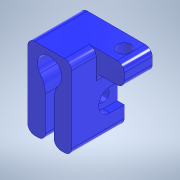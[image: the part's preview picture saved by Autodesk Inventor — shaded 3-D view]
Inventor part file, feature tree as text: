
AUTODESK INVENTOR PART (.ipt)
format: ipt  version: 2022 (Build 260153000, 153)  size: 223,744 bytes
history: native  units: in
note: dims shown in document units (in); Inventor stores cm internally (conversion verified against a paired STEP export)
features: sketch x4, extrude x4, hole x3, projected_geometry x2, plane x1, fillet x1
ambient origin geometry x8: Origin, YZ Plane, XZ Plane, XY Plane, X Axis, Y Axis, Z Axis, Center Point
bodies: Body1 (feature_tree)
feature tree (15):
  sketch  "Sketch14"  dims[d67=0.2756in d68=0.0984in]
  extrude  "Extrusion8"  Depth=0.0984in
  extrude  "Extrusion9"  Depth=0.2756in
  hole  "Hole12"  [1 undecoded]
  plane  "Work Plane4"
  sketch  "Sketch18"  dims[d69=0.2756in d70=0.2756in]
  extrude  "Extrusion13"  Depth=0.1969in
  hole  "Hole16"  [1 undecoded]
  hole  "Hole15"  [1 undecoded]
  extrude  "Extrusion14"  [1 undecoded]
  fillet  "Fillet3"  Radius=0.315in
  sketch  "Sketch19"  dims[d71=0.5906in d72=0.1969in]
  projected_geometry  "Projected Loop2"
  sketch  "Sketch20"  dims[d73=0.1969in d74=0.1969in d75=0.2756in d76=0.0in d77=0.315in d78=0.0in d79=0.1575in d80=0.2362in d81=0.1575in d82=0.0787in d83=90.0deg d84=0.315in d85=0.8108in d111=-0.1181in d112=0.315in d113=0.2165in d116=0.2362in d117=0.0in d126=0.1339in d127=0.2362in d128=0.2559in d129=0.0787in d130=90.0deg d131=0.315in d132=0.8108in d133=0.2362in d134=0.0in d135=0.0787in d139=0.315in d140=0.1575in d141=0.2362in d142=0.1575in d143=0.0787in d144=90.0deg d145=0.315in d146=0.8108in]
  projected_geometry  "Projected Loop3"
note: 4 required parameter values undecoded (feature->parameter linkage not recoverable at this tier; creation-order binding heuristic only, values carry confidence <= 0.55)
